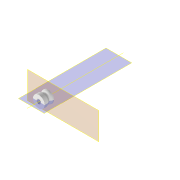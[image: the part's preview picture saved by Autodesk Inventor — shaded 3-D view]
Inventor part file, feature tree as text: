
AUTODESK INVENTOR PART (.ipt)
format: ipt  version: 2022 (Build 260153000, 153)  size: 129,024 bytes
history: native  units: mm
features: other x6, plane x2, sketch x2, extrude x1, revolve x1, fillet x1, reference x1
ambient origin geometry x8: Origin, YZ Plane, XZ Plane, XY Plane, X Axis, Y Axis, Z Axis, Center Point
bodies: Solid1 (feature_tree)
feature tree (14):
  plane  "Work Plane1"
  extrude  "Extrusion1"  TaperAngle=90.0deg  [1 undecoded]
  plane  "Work Plane2"
  other  "Work Axis1"
  revolve  "Revolution1"  [1 undecoded]
  fillet  "Fillet1"  [1 undecoded]
  sketch  "Sketch1"  dims[d0=8.0mm d1=0.0mm d2=90.0deg]
  reference  "Reference3"
  sketch  "Sketch2"  dims[d3=2.0mm d4=4.0mm]
  other  "<userpath>\Documents\Inventor\Guinardia\INVENTOR\Assembly_Guinardia_V0.iam"
  other  "Assembly_Guinardia_V0.iam"
  other  "20_Cube_Insert_Lightsheet_FEPTube_Rotating_hollomotor_v0:1"
  other  "10_Wellplate_base:1"
  other  "00_NEMA8:1"
note: 3 required parameter values undecoded (feature->parameter linkage not recoverable at this tier; creation-order binding heuristic only, values carry confidence <= 0.55)